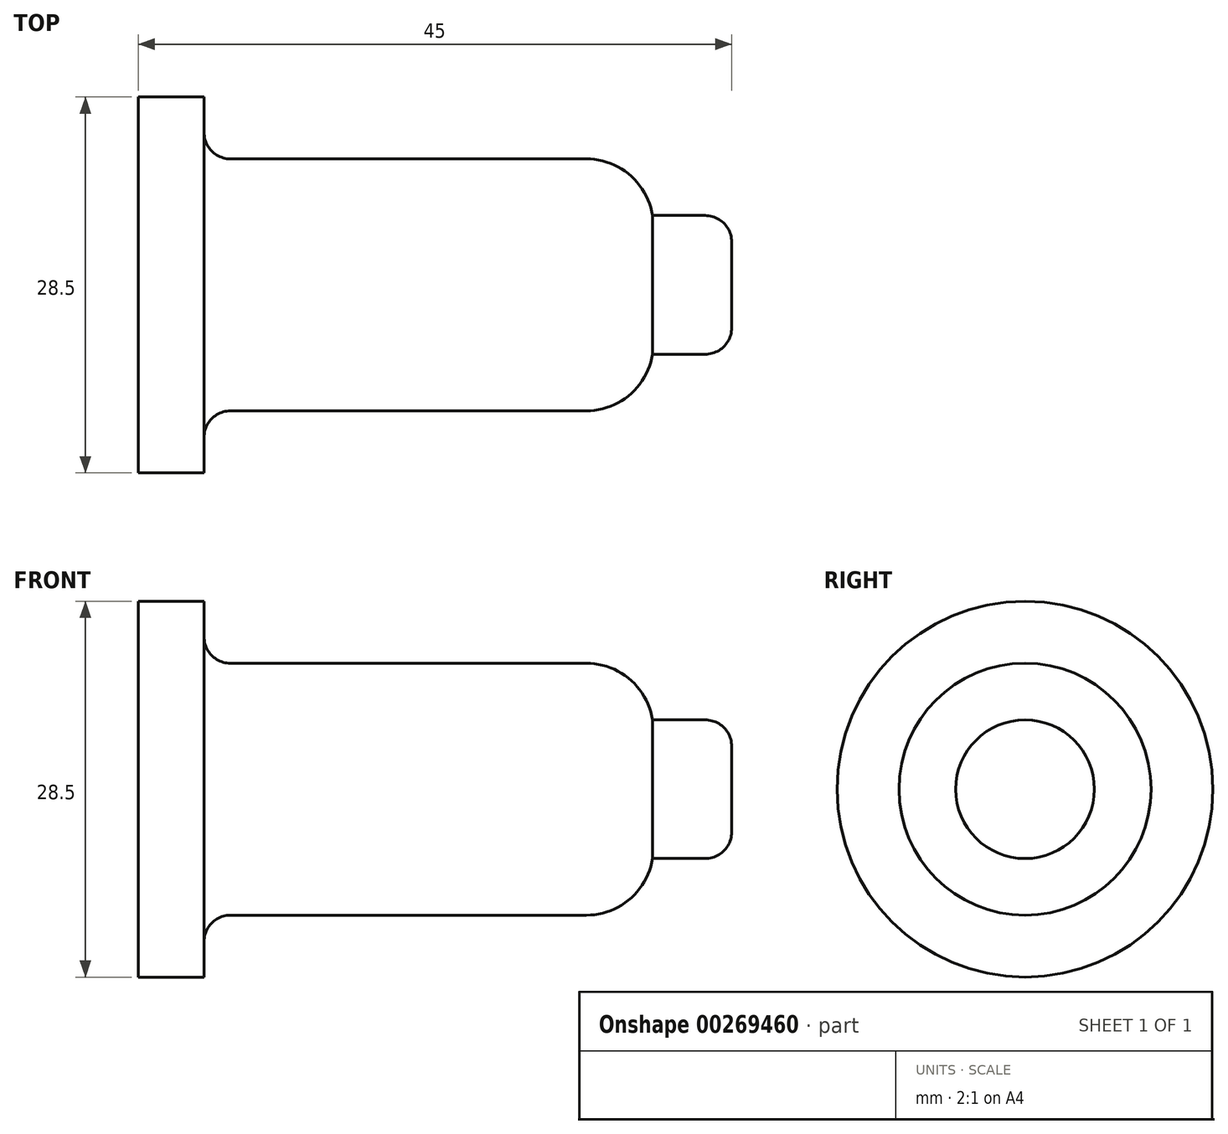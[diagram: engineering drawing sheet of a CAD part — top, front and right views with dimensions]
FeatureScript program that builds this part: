
annotation { "Feature Type Name" : "Feature", "Feature Type Description" : "" }
export const myFeature = defineFeature(function(context is Context, id is Id, definition is map)
    precondition{}
    {
        {
            var Q0;
            Q0=qCreatedBy(makeId("Right.planeOp"),FACE);
            var sketch = newSketch(context, id + "F0", { "sketchPlane" : qUnion([Q0])});
            skCircle(sketch, "E0", {"center": v(0, 0) * mm, "radius": 5.26 * mm});
            skSolve(sketch);
        }
        {
            var Q0;
            Q0 = qSketchRegion(id + "F0", true);
            extrude(context, id + "F12", {"entities" : qUnion([Q0]), "depth" : 45 * mm});
        }
        {
            var Q0;
            Q0=qCreatedBy(makeId("Right.planeOp"),FACE);
            var sketch = newSketch(context, id + "F1", { "sketchPlane" : qUnion([Q0])});
            skCircle(sketch, "E1", {"center": v(0, 0) * mm, "radius": 9.56 * mm});
            skSolve(sketch);
        }
        {
            var Q0;
            Q0 = qSketchRegion(id + "F1", true);
            extrude(context, id + "F2", {"entities" : qUnion([Q0]), "operationType" : NewBodyOperationType.ADD, "depth" : 39 * mm});
        }
        {
            var Q0;
            Q0=qCreatedBy(makeId("Right.planeOp"),FACE);
            var sketch = newSketch(context, id + "F13", { "sketchPlane" : qUnion([Q0])});
            skCircle(sketch, "E2", {"center": v(0, 0) * mm, "radius": 14.25 * mm});
            skSolve(sketch);
        }
        {
            var Q0;
            Q0 = qSketchRegion(id + "F13", true);
            extrude(context, id + "F3", {"entities" : qUnion([Q0]), "operationType" : NewBodyOperationType.ADD, "depth" : 5 * mm});
        }
        {
            var Q0;
            Q0=makeQuery(id+"F12.opExtrude","CAP_EDGE",EDGE,{"disambiguationData":[OSD([sQuery(id+"F0.wireOp",EDGE,"E0")])],"isStart":false});
            fillet(context, id + "F4", {"entities" : qUnion([Q0]), "radius" : 2 * mm, "tangentPropagation" : true, "allowEdgeOverflow" : false});
        }
        {
            var Q0;
            Q0=makeQuery(id+"F2.opExtrude","CAP_EDGE",EDGE,{"disambiguationData":[OSD([sQuery(id+"F1.wireOp",EDGE,"E1")])],"isStart":false});
            fillet(context, id + "F5", {"entities" : qUnion([Q0]), "radius" : 5.08 * mm, "tangentPropagation" : true, "allowEdgeOverflow" : false});
        }
        {
            var Q0;
            Q0=makeQuery(id+"F3.boolean.opBoolean","INTERSECT",EDGE,{"derivedFrom":[makeQuery(id+"F2.opExtrude","SWEPT_FACE",FACE,{"disambiguationData":[OSD([sQuery(id+"F1.wireOp",EDGE,"E1")])]}),makeQuery(id+"F3.opExtrude","CAP_FACE",FACE,{"disambiguationData":[OSD([sQuery(id+"F13.wireOp",EDGE,"E2")])],"isStart":false})]});
            fillet(context, id + "F6", {"entities" : qUnion([Q0]), "radius" : 2 * mm, "tangentPropagation" : true, "allowEdgeOverflow" : false});
        }
        {
            var Q0;
            Q0=qCreatedBy(makeId("Right.planeOp"),FACE);
            var sketch = newSketch(context, id + "F7", { "sketchPlane" : qUnion([Q0])});
            skCircle(sketch, "E3", {"center": v(0, 0) * mm, "radius": 0.77 * mm});
            skSolve(sketch);
        }
        {
            var Q0;
            Q0=sQuery(id+"F7.wireOp",EDGE,"E3");
            extrude(context, id + "F8", {"bodyType" : ToolBodyType.SURFACE, "surfaceEntities" : qUnion([Q0]), "depth" : 50 * mm});
        }
        {
            var Q0;
            Q0=makeQuery(id+"F8.opExtrude","SWEPT_BODY",BODY,{"disambiguationData":[OSD([sQuery(id+"F7.wireOp",EDGE,"E3")])]});
            deleteBodies(context, id + "F9", {"entities" : qUnion([Q0])});
        }
        {
            var Q0;
            Q0=qCreatedBy(makeId("Right.planeOp"),FACE);
            var sketch = newSketch(context, id + "F10", { "sketchPlane" : qUnion([Q0])});
            skLineSegment(sketch, "E4.bottom", {"start": v(0.93, -1) * mm, "end": v(-0.93, -1) * mm});
            skLineSegment(sketch, "E4.top", {"start": v(0.93, 1) * mm, "end": v(-0.93, 1) * mm});
            skLineSegment(sketch, "E4.left", {"start": v(0.93, -1) * mm, "end": v(0.93, 1) * mm});
            skLineSegment(sketch, "E4.right", {"start": v(-0.93, -1) * mm, "end": v(-0.93, 1) * mm});
            skPoint(sketch, "E4.middle", {"position": v(0, 0) * mm});
            skSolve(sketch);
        }
        {
            var Q0;
            Q0 = qSketchRegion(id + "F10", true);
            extrude(context, id + "F11", {"entities" : qUnion([Q0]), "operationType" : NewBodyOperationType.ADD, "depth" : 45 * mm});
        }
    });
